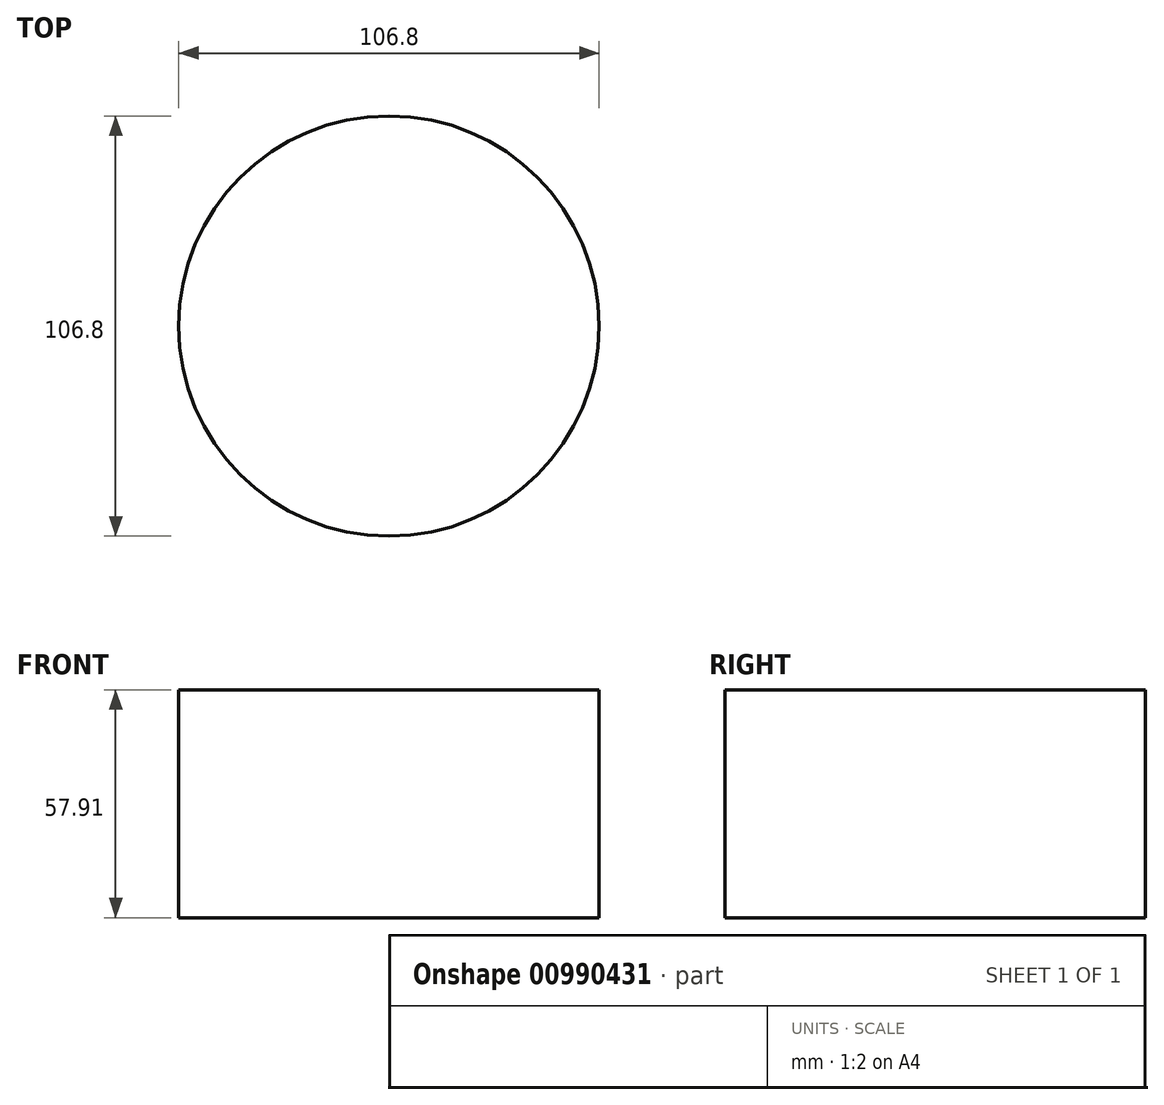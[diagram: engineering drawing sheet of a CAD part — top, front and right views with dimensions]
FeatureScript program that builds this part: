
annotation { "Feature Type Name" : "Feature", "Feature Type Description" : "" }
export const myFeature = defineFeature(function(context is Context, id is Id, definition is map)
    precondition{}
    {
        {
            var Q0;
            Q0=qCreatedBy(makeId("Top.planeOp"),FACE);
            var sketch = newSketch(context, id + "F0", { "sketchPlane" : qUnion([Q0])});
            skCircle(sketch, "E0", {"center": v(0, 0) * mm, "radius": 53.4 * mm});
            skSolve(sketch);
        }
        {
            var Q0;
            Q0=makeQuery(id+"F0.imprint","IMPRINT",FACE,{"disambiguationData":[TD([[makeQuery(id+"F0.imprint","IMPRINT",EDGE,{"derivedFrom":sQuery(id+"F0.wireOp",EDGE,"E0")}),1.0]])]});
            extrude(context, id + "F1", {"entities" : qUnion([Q0]), "depth" : 57.9 * mm, "offsetDistance" : 25.4 * mm});
        }
    });
